# Revit family: Drain_Drip_Open_Sight_6x12_Inch-Zurn-Z1721
name_source: partatom
category: Plumbing Fixtures
units: mm (PartAtom-declared; Revit-internal decimal feet)

## family parameters
Always vertical = Yes
Cut with Voids When Loaded = No
Maintain Annotation Orientation = No
OmniClass Number = 23.70.50.21.24.14
OmniClass Title = Deck Waste Water Drains
Part Type = Normal
Room Calculation Point = No
Round Connector Dimension = Use Radius
Shared = No
Work Plane-Based = No

## types (12) — shared parameters
Approx. Wt. Lbs = 30 "
Assembly Code = D2030300
Body Height_E = 10 "
CW Connection = No
Default Elevation = 25 "
Description = 6 X 12 [152 X 305] OPEN SIGHT DRIP DRAIN
HW Connection = No
Manufacturer = Zurn Water, LLC
Manufacturer Brand = Zurn
Model = Z1721
Modified Date = 12/19/2025
Product Documentation Link = https://files.zurn.com
Product Page URL = https://www.zurn.com
Product data URL = https://www.bimobject.com
URL = www.zurn.com
Vent Connection = No
WFU = 1
Waste Connection = Yes
Width_1 = 6 "
Width_2 = 12 "
zero-valued in all types: CWFU, HWFU

## per-type parameters (varying)
| type | Main Material | Pipe Size A (Actual Radius) | Pipe Size A (Diameter) | Pipe Size A (Inner Radius) | Pipe Size A (Nominal Radius) | Type Comments |
| Z1721-3BW | Steel - Zurn - Stainless - Type - 304 | 1.75 " | 3 " | 1.534 " | 1.5 " | Z1721-3 Inch-Butt Weld Outlet |
| Z1721-4BW | Steel - Zurn - Stainless - Type - 304 | 2.25 " | 4 " | 2.013 " | 2 " | Z1721-4 Inch-Butt Weld Outlet |
| Z1721-6BW | Steel - Zurn - Stainless - Type - 304 | 3.313 " | 6 " | 3.033 " | 3 " | Z1721-6 Inch-Butt Weld Outlet |
| Z1721-3IP | Steel - Zurn - Stainless - Type - 304 | 1.75 " | 3 " | 1.534 " | 1.5 " | Z1721-3 Inch-Threaded Outlet |
| Z1721-4IP | Steel - Zurn - Stainless - Type - 304 | 2.25 " | 4 " | 2.013 " | 2 " | Z1721-4 Inch-Threaded Outlet |
| Z1721-6IP | Steel - Zurn - Stainless - Type - 304 | 3.313 " | 6 " | 3.033 " | 3 " | Z1721-6 Inch-Threaded Outlet |
| ZM1721-3BW | Steel - Zurn - Stainless - Type - 316 | 1.75 " | 3 " | 1.534 " | 1.5 " | ZM1721-3 Inch-Butt Weld Outlet |
| ZM1721-4BW | Steel - Zurn - Stainless - Type - 316 | 2.25 " | 4 " | 2.013 " | 2 " | ZM1721-4 Inch-Butt Weld Outlet |
| ZM1721-6BW | Steel - Zurn - Stainless - Type - 316 | 3.313 " | 6 " | 3.033 " | 3 " | ZM1721-6 Inch-Butt Weld Outlet |
| ZM1721-3IP | Steel - Zurn - Stainless - Type - 316 | 1.75 " | 3 " | 1.534 " | 1.5 " | ZM1721-3 Inch-Threaded Outlet |
| ZM1721-4IP | Steel - Zurn - Stainless - Type - 316 | 2.25 " | 4 " | 2.013 " | 2 " | ZM1721-4 Inch-Threaded Outlet |
| ZM1721-6IP | Steel - Zurn - Stainless - Type - 316 | 3.313 " | 6 " | 3.033 " | 3 " | ZM1721-6 Inch-Threaded Outlet |

## geometry (parser evidence)
native form markers: Blend x4, Sweep x1
no freeform markers — native parametric forms only
